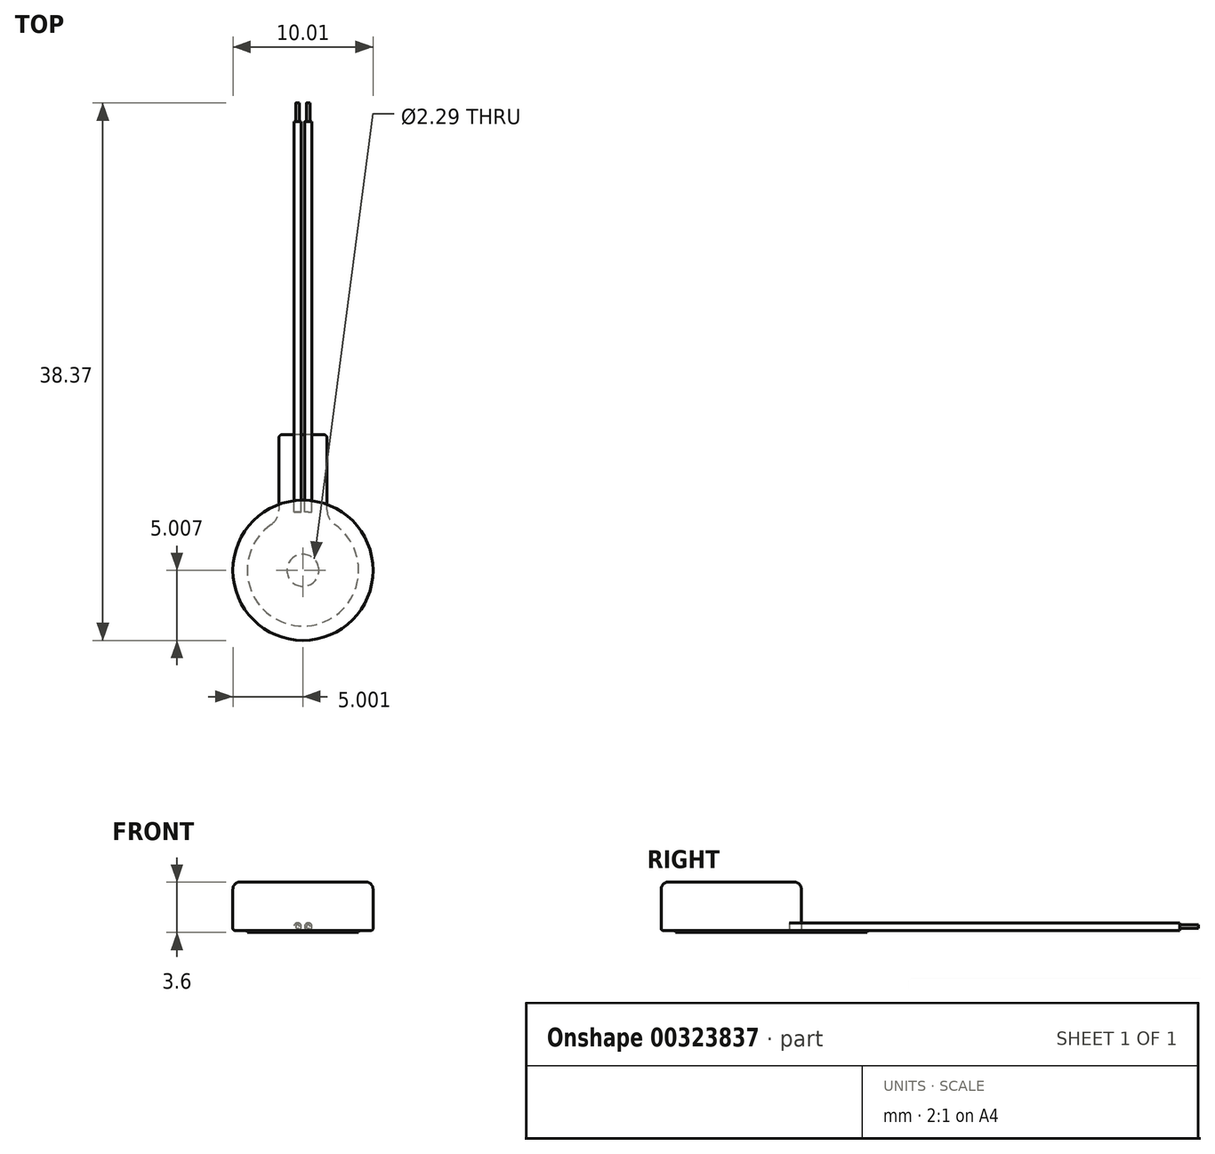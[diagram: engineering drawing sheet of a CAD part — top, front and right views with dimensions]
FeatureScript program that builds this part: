
annotation { "Feature Type Name" : "Feature", "Feature Type Description" : "" }
export const myFeature = defineFeature(function(context is Context, id is Id, definition is map)
    precondition{}
    {
        {
            var Q0;
            Q0=qCreatedBy(makeId("Top.planeOp"),FACE);
            var sketch = newSketch(context, id + "F0", { "sketchPlane" : qUnion([Q0])});
            skCircle(sketch, "E0", {"center": v(-16.2, 14.9) * mm, "radius": 5 * mm});
            skSolve(sketch);
        }
        {
            var Q0;
            Q0 = qSketchRegion(id + "F0", true);
            extrude(context, id + "F1", {"entities" : qUnion([Q0]), "depth" : 3.45 * mm});
        }
        {
            var Q0;
            Q0=makeQuery(id+"F1.opExtrude","CAP_FACE",FACE,{"disambiguationData":[OSD([sQuery(id+"F0.wireOp",EDGE,"E0")])],"isStart":true});
            var sketch = newSketch(context, id + "F2", { "sketchPlane" : qUnion([Q0])});
            skCircle(sketch, "E1.0", {"center": v(-16.2, -14.9) * mm, "radius": 5 * mm});
            skCircle(sketch, "E2", {"center": v(-16.2, -14.9) * mm, "radius": 1.14 * mm});
            skArc(sketch, "E3", {"start": v(-13.94, -18.16) * mm, "mid": v(-16.2, -10.92) * mm, "end": v(-18.48, -18.16) * mm});
            skLineSegment(sketch, "E4", {"start": v(-14.49, -19.2) * mm, "end": v(-14.49, -24.33) * mm});
            skLineSegment(sketch, "E5", {"start": v(-14.74, -24.59) * mm, "end": v(-17.68, -24.59) * mm});
            skLineSegment(sketch, "E6", {"start": v(-17.93, -24.33) * mm, "end": v(-17.93, -19.2) * mm});
            skPoint(sketch, "E7.visualSharp", {"position": v(-17.93, -18.48) * mm});
            skArc(sketch, "E7.filletArc", {"start": v(-17.93, -19.2) * mm, "mid": v(-18.07, -18.62) * mm, "end": v(-18.48, -18.16) * mm});
            skPoint(sketch, "E8.visualSharp", {"position": v(-14.49, -18.48) * mm});
            skArc(sketch, "E8.filletArc", {"start": v(-13.94, -18.16) * mm, "mid": v(-14.34, -18.62) * mm, "end": v(-14.49, -19.2) * mm});
            skPoint(sketch, "E9.visualSharp", {"position": v(-17.93, -24.59) * mm});
            skArc(sketch, "E9.filletArc", {"start": v(-17.93, -24.33) * mm, "mid": v(-17.86, -24.51) * mm, "end": v(-17.68, -24.59) * mm});
            skPoint(sketch, "E10.visualSharp", {"position": v(-14.49, -24.59) * mm});
            skArc(sketch, "E10.filletArc", {"start": v(-14.74, -24.59) * mm, "mid": v(-14.56, -24.51) * mm, "end": v(-14.49, -24.33) * mm});
            skSolve(sketch);
        }
        {
            var Q0;
            Q0=makeQuery(id+"F2.imprint","IMPRINT",FACE,{"disambiguationData":[TD([[makeQuery(id+"F2.imprint","IMPRINT",EDGE,{"derivedFrom":sQuery(id+"F2.wireOp",EDGE,"E2")}),-1.0]])]});
            var Q1;
            Q1=makeQuery(id+"F2.imprint","IMPRINT",FACE,{"disambiguationData":[TD([[makeQuery(id+"F2.imprint","IMPRINT",EDGE,{"derivedFrom":sQuery(id+"F2.wireOp",EDGE,"E5")}),-1.0]])]});
            extrude(context, id + "F3", {"entities" : qUnion([Q0, Q1]), "depth" : 0.15 * mm});
        }
        {
            var Q0;
            Q0=qCreatedBy(makeId("Front.planeOp"),FACE);
            cPlane(context, id + "F4", {"entities" : qUnion([Q0]), "cplaneType" : CPlaneType.OFFSET, "offset" : 20.32 * mm, "oppositeDirection" : true, "width" : 152.4 * mm, "height" : 152.4 * mm});
        }
        {
            var Q0;
            Q0=qCreatedBy(id+"F4.planeOp",FACE);
            var sketch = newSketch(context, id + "F5", { "sketchPlane" : qUnion([Q0])});
            skCircle(sketch, "E11", {"center": v(-16.59, 0.27) * mm, "radius": 0.27 * mm});
            skCircle(sketch, "E12", {"center": v(-15.83, 0.27) * mm, "radius": 0.27 * mm});
            skLineSegment(sketch, "E13.0", {"start": v(-21.21, 0) * mm, "end": v(-11.2, 0) * mm});
            skLineSegment(sketch, "E14.0.0", {"start": v(-17.68, 0) * mm, "end": v(-14.74, 0) * mm});
            skLineSegment(sketch, "E14.0.1", {"start": v(-14.74, 0) * mm, "end": v(-14.74, -0.15) * mm});
            skLineSegment(sketch, "E14.0.2", {"start": v(-14.74, -0.15) * mm, "end": v(-17.68, -0.15) * mm});
            skLineSegment(sketch, "E14.0.3", {"start": v(-17.68, -0.15) * mm, "end": v(-17.68, 0) * mm});
            skPoint(sketch, "E15.0", {"position": v(-14.49, 0) * mm});
            skLineSegment(sketch, "E16", {"start": v(-14.74, 0) * mm, "end": v(-14.74, 1.03) * mm, "construction": true});
            skLineSegment(sketch, "E17", {"start": v(-14.74, 1.03) * mm, "end": v(-17.68, 1.03) * mm, "construction": true});
            skLineSegment(sketch, "E18", {"start": v(-17.68, 1.03) * mm, "end": v(-17.68, 0) * mm, "construction": true});
            skPoint(sketch, "E19", {"position": v(-16.2, 1.03) * mm});
            skSolve(sketch);
        }
        {
            var Q0;
            Q0=makeQuery(id+"F5.imprint","IMPRINT",FACE,{"disambiguationData":[TD([[makeQuery(id+"F5.imprint","IMPRINT",EDGE,{"derivedFrom":sQuery(id+"F5.wireOp",EDGE,"E11")}),1.0]])]});
            extrude(context, id + "F6", {"entities" : qUnion([Q0]), "depth" : 1.27 * mm});
        }
        {
            var Q0;
            Q0=makeQuery(id+"F5.imprint","IMPRINT",FACE,{"disambiguationData":[TD([[makeQuery(id+"F5.imprint","IMPRINT",EDGE,{"derivedFrom":sQuery(id+"F5.wireOp",EDGE,"E12")}),1.0]])]});
            extrude(context, id + "F7", {"entities" : qUnion([Q0]), "depth" : 1.27 * mm});
        }
        {
            var Q0;
            Q0=makeQuery(id+"F5.imprint","IMPRINT",FACE,{"disambiguationData":[TD([[makeQuery(id+"F5.imprint","IMPRINT",EDGE,{"derivedFrom":sQuery(id+"F5.wireOp",EDGE,"E11")}),1.0]])]});
            extrude(context, id + "F8", {"entities" : qUnion([Q0]), "operationType" : NewBodyOperationType.ADD, "oppositeDirection" : true, "depth" : 27.94 * mm});
        }
        {
            var Q0;
            Q0=makeQuery(id+"F5.imprint","IMPRINT",FACE,{"disambiguationData":[TD([[makeQuery(id+"F5.imprint","IMPRINT",EDGE,{"derivedFrom":sQuery(id+"F5.wireOp",EDGE,"E12")}),1.0]])]});
            extrude(context, id + "F9", {"entities" : qUnion([Q0]), "operationType" : NewBodyOperationType.ADD, "oppositeDirection" : true, "depth" : 27.94 * mm});
        }
        {
            var Q0;
            Q0=makeQuery(id+"F8.opExtrude","CAP_FACE",FACE,{"disambiguationData":[OSD([sQuery(id+"F5.wireOp",EDGE,"E11")])],"isStart":false});
            var sketch = newSketch(context, id + "F10", { "sketchPlane" : qUnion([Q0])});
            skCircle(sketch, "E20.0.0", {"center": v(15.83, 0.27) * mm, "radius": 0.27 * mm});
            skCircle(sketch, "E21.0", {"center": v(16.59, 0.27) * mm, "radius": 0.27 * mm});
            skCircle(sketch, "E22", {"center": v(15.83, 0.27) * mm, "radius": 0.13 * mm});
            skCircle(sketch, "E23", {"center": v(16.59, 0.27) * mm, "radius": 0.13 * mm});
            skSolve(sketch);
        }
        {
            var Q0;
            Q0=makeQuery(id+"F10.imprint","IMPRINT",FACE,{"disambiguationData":[TD([[makeQuery(id+"F10.imprint","IMPRINT",EDGE,{"derivedFrom":sQuery(id+"F10.wireOp",EDGE,"E20.0.0")}),1.0]])]});
            extrude(context, id + "F11", {"entities" : qUnion([Q0]), "operationType" : NewBodyOperationType.REMOVE, "oppositeDirection" : true, "depth" : 1.33 * mm});
        }
        {
            var Q0;
            Q0=makeQuery(id+"F10.imprint","IMPRINT",FACE,{"disambiguationData":[TD([[makeQuery(id+"F10.imprint","IMPRINT",EDGE,{"derivedFrom":sQuery(id+"F10.wireOp",EDGE,"E21.0")}),-1.0]])]});
            extrude(context, id + "F12", {"entities" : qUnion([Q0]), "operationType" : NewBodyOperationType.REMOVE, "oppositeDirection" : true, "depth" : 1.33 * mm});
        }
        {
            var Q0;
            Q0=makeQuery(id+"F1.opExtrude","CAP_EDGE",EDGE,{"disambiguationData":[OSD([sQuery(id+"F0.wireOp",EDGE,"E0")])],"isStart":false});
            fillet(context, id + "F13", {"entities" : qUnion([Q0]), "radius" : 0.5 * mm, "tangentPropagation" : true, "allowEdgeOverflow" : false});
        }
        {
            var Q0;
            Q0=makeQuery(id+"F1.opExtrude","CAP_EDGE",EDGE,{"disambiguationData":[OSD([sQuery(id+"F0.wireOp",EDGE,"E0")])],"isStart":true});
            fillet(context, id + "F14", {"entities" : qUnion([Q0]), "radius" : 0.13 * mm, "tangentPropagation" : true, "allowEdgeOverflow" : false});
        }
    });
